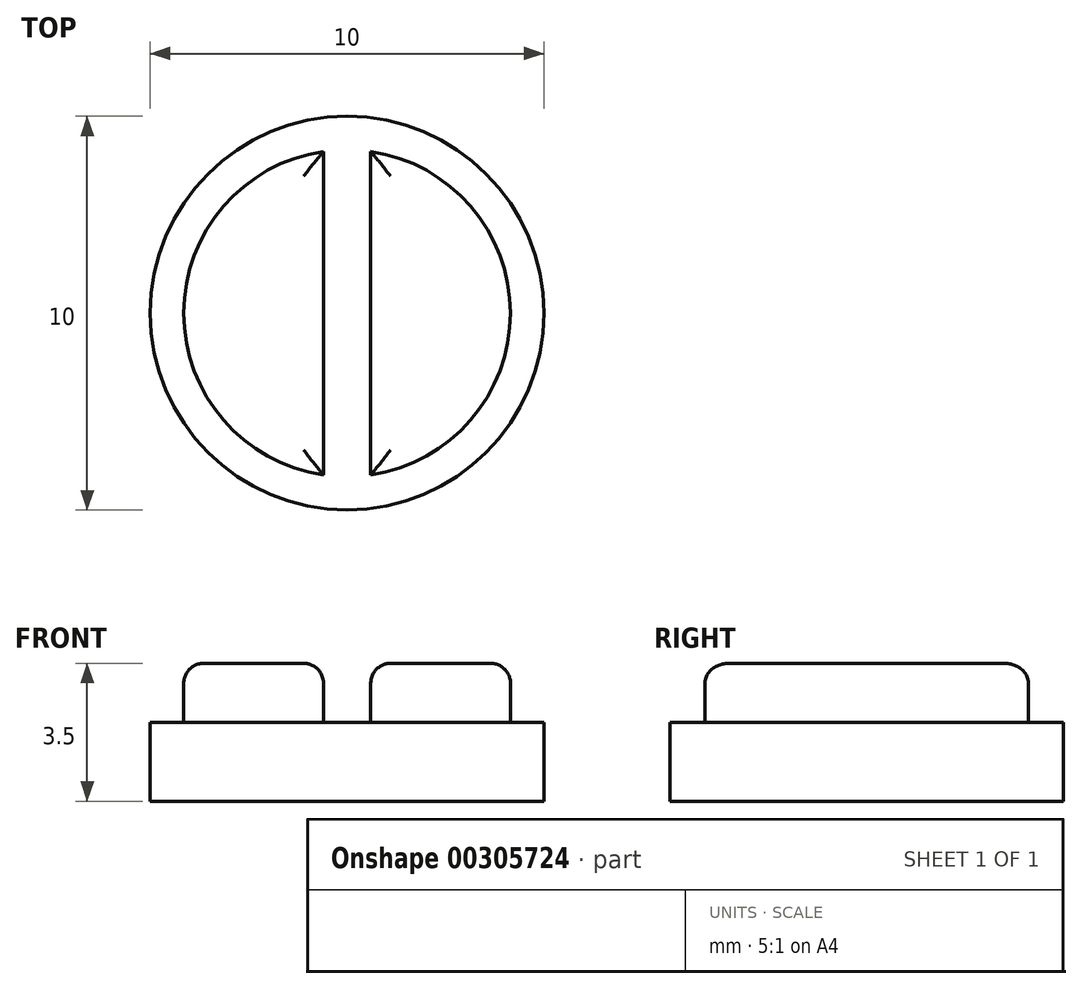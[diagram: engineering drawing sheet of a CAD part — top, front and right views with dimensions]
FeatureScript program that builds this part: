
annotation { "Feature Type Name" : "Feature", "Feature Type Description" : "" }
export const myFeature = defineFeature(function(context is Context, id is Id, definition is map)
    precondition{}
    {
        {
            var Q0;
            Q0=qCreatedBy(makeId("Top.planeOp"),FACE);
            var sketch = newSketch(context, id + "F0", { "sketchPlane" : qUnion([Q0])});
            skCircle(sketch, "E0", {"center": v(0, 0) * mm, "radius": 5 * mm});
            skSolve(sketch);
        }
        {
            var Q0;
            Q0 = qSketchRegion(id + "F0", true);
            extrude(context, id + "F1", {"entities" : qUnion([Q0]), "depth" : 2 * mm});
        }
        {
            var Q0;
            Q0=makeQuery(id+"F1.opExtrude","CAP_FACE",FACE,{"disambiguationData":[OSD([sQuery(id+"F0.wireOp",EDGE,"E0")])],"isStart":false});
            var sketch = newSketch(context, id + "F2", { "sketchPlane" : qUnion([Q0])});
            skCircle(sketch, "E1", {"center": v(0, 0) * mm, "radius": 4.15 * mm});
            skLineSegment(sketch, "E2.bottom", {"start": v(0.6, -4.1) * mm, "end": v(-0.6, -4.1) * mm});
            skLineSegment(sketch, "E2.top", {"start": v(0.6, 4.1) * mm, "end": v(-0.6, 4.1) * mm});
            skLineSegment(sketch, "E2.left", {"start": v(0.6, -4.1) * mm, "end": v(0.6, 4.1) * mm});
            skLineSegment(sketch, "E2.right", {"start": v(-0.6, -4.1) * mm, "end": v(-0.6, 4.1) * mm});
            skSolve(sketch);
        }
        {
            var Q0;
            {var subQ0=sQuery(id+"F2.wireOp",EDGE,"E2.right");Q0=makeQuery(id+"F2.imprint","IMPRINT",FACE,{"disambiguationData":[TD([[makeQuery(id+"F2.imprint","IMPRINT",EDGE,{"derivedFrom":subQ0}),1.0]])]});}
            var Q1;
            {var subQ0=sQuery(id+"F2.wireOp",EDGE,"E2.left");Q1=makeQuery(id+"F2.imprint","IMPRINT",FACE,{"disambiguationData":[TD([[makeQuery(id+"F2.imprint","IMPRINT",EDGE,{"derivedFrom":subQ0}),-1.0]])]});}
            extrude(context, id + "F3", {"entities" : qUnion([Q0, Q1]), "operationType" : NewBodyOperationType.ADD, "depth" : 1.5 * mm});
        }
        {
            var Q0;
            Q0=makeQuery(id+"F3.opExtrude","CAP_EDGE",EDGE,{"disambiguationData":[OSD([sQuery(id+"F2.wireOp",EDGE,"E2.right")])],"isStart":false});
            var Q1;
            {var subQ0=sQuery(id+"F2.wireOp",EDGE,"E2.right");var subQ1=sQuery(id+"F2.wireOp",EDGE,"E1");Q1=makeQuery(id+"F3.opExtrude","CAP_EDGE",EDGE,{"disambiguationData":[OSD([subQ1]),TDD([makeQuery(id+"F2.imprint","IMPRINT",EDGE,{"disambiguationData":[TD([[makeQuery(id+"F2.imprint","INTERSECT",VERTEX,{"derivedFrom":[subQ1,sQuery(id+"F2.wireOp",EDGE,"E2.bottom"),subQ0]}),1.0]])],"derivedFrom":subQ1})])],"isStart":false});}
            var Q2;
            Q2=makeQuery(id+"F3.opExtrude","CAP_EDGE",EDGE,{"disambiguationData":[OSD([sQuery(id+"F2.wireOp",EDGE,"E2.left")])],"isStart":false});
            var Q3;
            {var subQ0=sQuery(id+"F2.wireOp",EDGE,"E2.left");var subQ1=sQuery(id+"F2.wireOp",EDGE,"E1");Q3=makeQuery(id+"F3.opExtrude","CAP_EDGE",EDGE,{"disambiguationData":[OSD([subQ1]),TDD([makeQuery(id+"F2.imprint","IMPRINT",EDGE,{"disambiguationData":[TD([[makeQuery(id+"F2.imprint","INTERSECT",VERTEX,{"derivedFrom":[subQ1,sQuery(id+"F2.wireOp",EDGE,"E2.bottom"),subQ0]}),-1.0]])],"derivedFrom":subQ1})])],"isStart":false});}
            fillet(context, id + "F4", {"entities" : qUnion([Q0, Q1, Q2, Q3]), "radius" : 0.5 * mm, "tangentPropagation" : true, "allowEdgeOverflow" : false});
        }
    });
